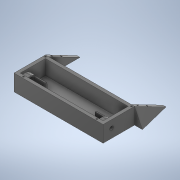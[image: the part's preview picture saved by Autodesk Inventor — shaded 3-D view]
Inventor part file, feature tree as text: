
AUTODESK INVENTOR PART (.ipt)
format: ipt  version: 2020 (Build 240168000, 168)  size: 350,720 bytes
history: native  units: in
note: dims shown in document units (in); Inventor stores cm internally (conversion verified against a paired STEP export)
features: extrude x10, sketch x9, projected_geometry x7, mirror x3, plane x2
ambient origin geometry x8: Origin, YZ Plane, XZ Plane, XY Plane, X Axis, Y Axis, Z Axis, Center Point
bodies: Solid1 (feature_tree)
feature tree (31):
  extrude  "Extrusion1"  Depth=2.3622in
  extrude  "Extrusion2"  Depth=1.1024in TaperAngle=0.0deg
  extrude  "Extrusion5"  Depth=0.0787in
  extrude  "Extrusion6"  Depth=0.7874in TaperAngle=0.0deg
  extrude  "Extrusion7"  Depth=0.6693in
  mirror  "Mirror2"
  extrude  "Extrusion12"  Depth=0.5906in
  mirror  "Mirror5"
  extrude  "Extrusion13"  Depth=1.8898in
  plane  "Work Plane2"
  extrude  "Extrusion14"  Depth=0.6299in
  mirror  "Mirror8"
  extrude  "Extrusion15"  Depth=0.3937in
  extrude  "Extrusion16"  Depth=0.4724in
  sketch  "Sketch2"  dims[d0=6.6929in d1=2.3622in]
  projected_geometry  "Projected Loop1"
  sketch  "Sketch7"  dims[d2=0.1181in d3=0.0in d5=1.1024in d6=0.0in]
  sketch  "Sketch8"  dims[d18=0.6693in d20=0.0787in]
  projected_geometry  "Projected Loop5"
  sketch  "Sketch9"  dims[d21=0.4429in d22=0.0in d25=0.7874in d26=0.0in]
  sketch  "Sketch15"  dims[d27=0.2756in d28=0.6693in]
  projected_geometry  "Projected Loop6"
  sketch  "Sketch16"  dims[d30=0.4626in d31=0.0in d32=0.5906in]
  projected_geometry  "Projected Loop7"
  sketch  "Sketch19"  dims[d36=6.2205in d37=1.8898in]
  plane  "Work Plane3"
  sketch  "Sketch20"  dims[d40=0.7874in d41=0.6299in]
  projected_geometry  "Projected Loop8"
  projected_geometry  "Projected Loop9"
  sketch  "Sketch21"  dims[d55=0.6102in d62=0.3937in d63=0.4724in d64=0.2362in d67=2.3622in d68=0.2362in d69=0.0in d71=2.3622in d72=0.0in d73=2.3622in d74=0.0in d75=0.1142in d76=0.3937in d77=0.1142in d78=0.7874in d79=0.2559in d80=0.0in d82=0.1181in d83=0.1181in d84=0.1181in d85=0.1142in d86=0.1142in d87=0.5906in d88=0.2559in d89=0.0in d50=0.0197in d51=0.0344in d52=0.0197in d53=0.0344in]
  projected_geometry  "Projected Loop10"
